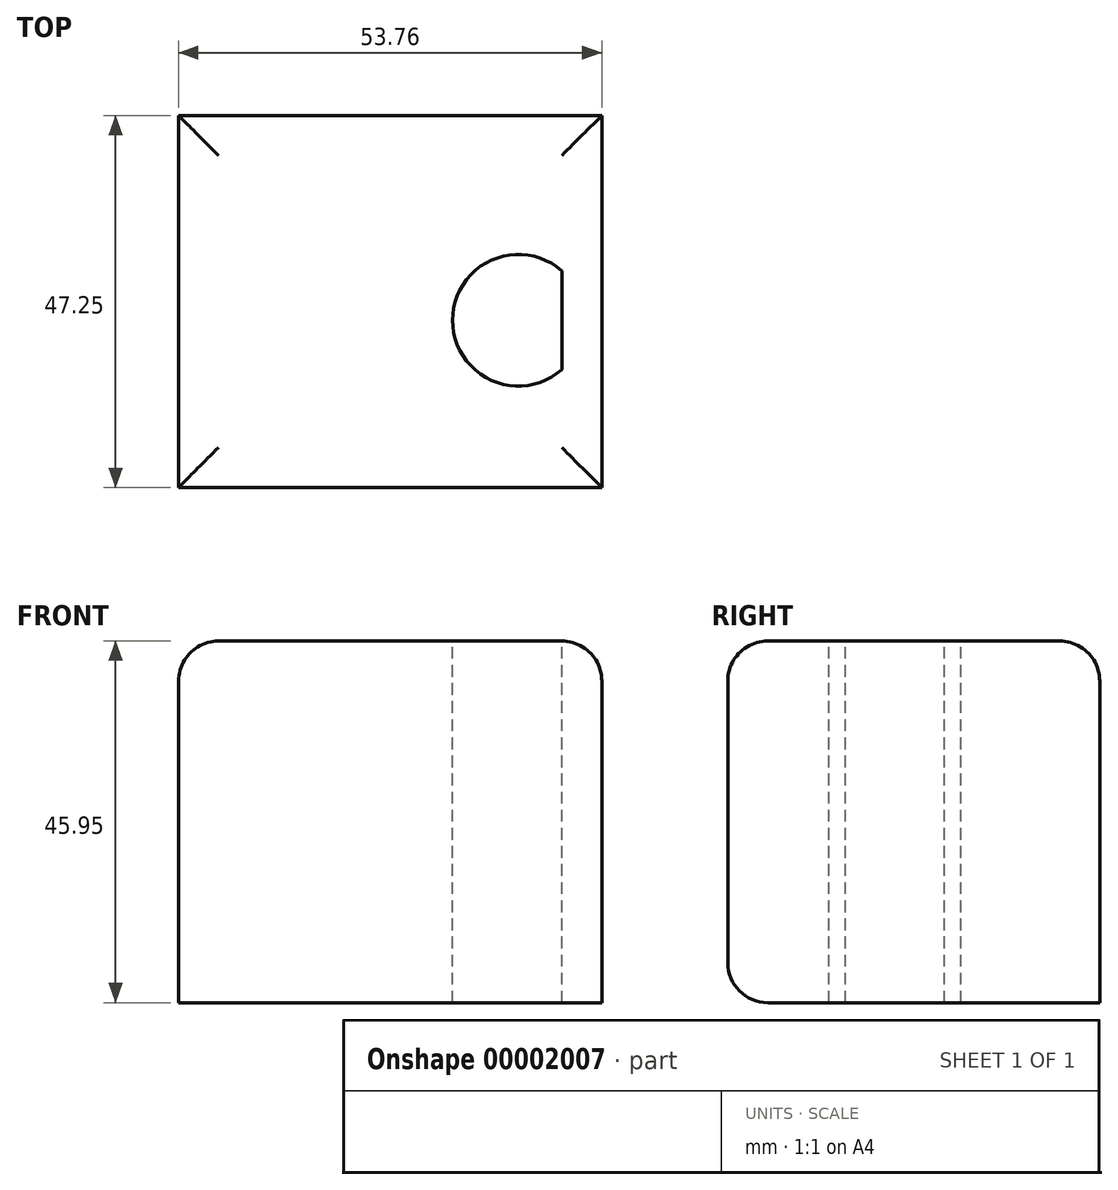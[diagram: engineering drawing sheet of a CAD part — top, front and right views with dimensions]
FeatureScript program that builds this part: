
annotation { "Feature Type Name" : "Feature", "Feature Type Description" : "" }
export const myFeature = defineFeature(function(context is Context, id is Id, definition is map)
    precondition{}
    {
        {
            var Q0;
            Q0=qCreatedBy(makeId("Top.planeOp"),FACE);
            var sketch = newSketch(context, id + "F0", { "sketchPlane" : qUnion([Q0])});
            skLineSegment(sketch, "E0.bottom", {"start": v(-60.68, -33) * mm, "end": v(-6.92, -33) * mm});
            skLineSegment(sketch, "E0.top", {"start": v(-60.68, 14.24) * mm, "end": v(-6.92, 14.24) * mm});
            skLineSegment(sketch, "E0.left", {"start": v(-60.68, -33) * mm, "end": v(-60.68, 14.24) * mm});
            skLineSegment(sketch, "E0.right", {"start": v(-6.92, -33) * mm, "end": v(-6.92, 14.24) * mm});
            skSolve(sketch);
        }
        {
            var Q0;
            Q0=makeQuery(id+"F0.imprint","IMPRINT",FACE,{"disambiguationData":[TD([[makeQuery(id+"F0.imprint","IMPRINT",EDGE,{"derivedFrom":sQuery(id+"F0.wireOp",EDGE,"E0.bottom")}),1.0]])]});
            extrude(context, id + "F1", {"entities" : qUnion([Q0]), "depth" : 45.95 * mm});
        }
        {
            var Q0;
            Q0=makeQuery(id+"F1.opExtrude","CAP_EDGE",EDGE,{"disambiguationData":[OSD([sQuery(id+"F0.wireOp",EDGE,"E0.right")])],"isStart":false});
            var Q1;
            Q1=makeQuery(id+"F1.opExtrude","CAP_EDGE",EDGE,{"disambiguationData":[OSD([sQuery(id+"F0.wireOp",EDGE,"E0.bottom")])],"isStart":false});
            var Q2;
            Q2=makeQuery(id+"F1.opExtrude","CAP_EDGE",EDGE,{"disambiguationData":[OSD([sQuery(id+"F0.wireOp",EDGE,"E0.left")])],"isStart":false});
            var Q3;
            Q3=makeQuery(id+"F1.opExtrude","CAP_EDGE",EDGE,{"disambiguationData":[OSD([sQuery(id+"F0.wireOp",EDGE,"E0.top")])],"isStart":false});
            fillet(context, id + "F2", {"entities" : qUnion([Q0, Q1, Q2, Q3]), "radius" : 5.08 * mm, "tangentPropagation" : true, "allowEdgeOverflow" : false});
        }
        {
            var Q0;
            Q0=makeQuery(id+"F1.opExtrude","CAP_FACE",FACE,{"disambiguationData":[OSD([sQuery(id+"F0.wireOp",EDGE,"E0.bottom"),sQuery(id+"F0.wireOp",EDGE,"E0.top"),sQuery(id+"F0.wireOp",EDGE,"E0.left"),sQuery(id+"F0.wireOp",EDGE,"E0.right")])],"isStart":false});
            var sketch = newSketch(context, id + "F3", { "sketchPlane" : qUnion([Q0])});
            skCircle(sketch, "E1", {"center": v(-17.52, -11.77) * mm, "radius": 8.36 * mm});
            skSolve(sketch);
        }
        {
            var Q0;
            {var subQ0=sQuery(id+"F0.wireOp",EDGE,"E0.right");var subQ1=makeQuery(id+"F2.opFillet","BLEND_EDGE",EDGE,{"blendedFrom":[makeQuery(id+"F1.opExtrude","CAP_EDGE",EDGE,{"disambiguationData":[OSD([subQ0])],"isStart":false}),makeQuery(id+"F1.opExtrude","CAP_FACE",FACE,{"disambiguationData":[OSD([sQuery(id+"F0.wireOp",EDGE,"E0.bottom"),sQuery(id+"F0.wireOp",EDGE,"E0.top"),sQuery(id+"F0.wireOp",EDGE,"E0.left"),subQ0])],"isStart":false})],"blendedInto":[makeQuery(id+"F1.opExtrude","CAP_FACE",FACE,{"disambiguationData":[OSD([sQuery(id+"F0.wireOp",EDGE,"E0.bottom"),sQuery(id+"F0.wireOp",EDGE,"E0.top"),sQuery(id+"F0.wireOp",EDGE,"E0.left"),subQ0])],"isStart":false})]});var subQ2=sQuery(id+"F3.wireOp",EDGE,"E1");var subQ4=makeQuery(id+"F3.imprint","INTERSECT",VERTEX,{"disambiguationData":[OD(0.0)],"derivedFrom":[subQ1,subQ2]});Q0=makeQuery(id+"F3.imprint","IMPRINT",FACE,{"disambiguationData":[TD([[makeQuery(id+"F3.imprint","IMPRINT",EDGE,{"disambiguationData":[TD([[subQ4,1.0]])],"derivedFrom":subQ2}),1.0]])]});}
            extrude(context, id + "F4", {"entities" : qUnion([Q0]), "operationType" : NewBodyOperationType.REMOVE, "oppositeDirection" : true, "depth" : 66.15 * mm});
        }
        {
            var Q0;
            Q0=makeQuery(id+"F1.opExtrude","CAP_EDGE",EDGE,{"disambiguationData":[OSD([sQuery(id+"F0.wireOp",EDGE,"E0.bottom")])],"isStart":true});
            fillet(context, id + "F5", {"entities" : qUnion([Q0]), "tangentPropagation" : true, "radius" : 5.08 * mm, "defaultsChanged" : false, "vertexSettings" : [], "allowEdgeOverflow" : false});
        }
    });
